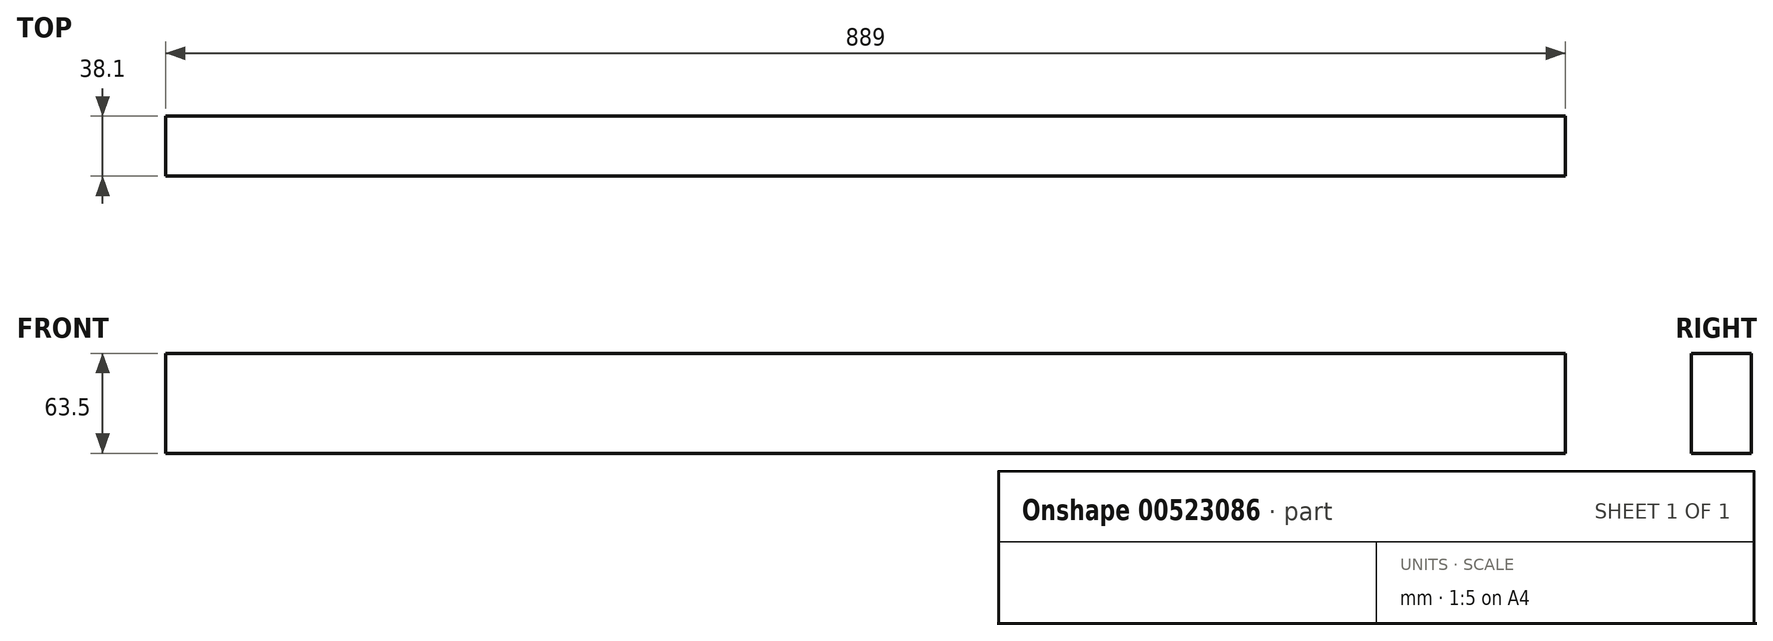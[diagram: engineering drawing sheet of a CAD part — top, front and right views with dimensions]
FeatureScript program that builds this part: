
annotation { "Feature Type Name" : "Feature", "Feature Type Description" : "" }
export const myFeature = defineFeature(function(context is Context, id is Id, definition is map)
    precondition{}
    {
        {
            var Q0;
            Q0=qCreatedBy(makeId("Top.planeOp"),FACE);
            var sketch = newSketch(context, id + "F0", { "sketchPlane" : qUnion([Q0])});
            skLineSegment(sketch, "E0.bottom", {"start": v(0, 0) * mm, "end": v(889, 0) * mm});
            skLineSegment(sketch, "E0.top", {"start": v(0, 38.1) * mm, "end": v(889, 38.1) * mm});
            skLineSegment(sketch, "E0.left", {"start": v(0, 0) * mm, "end": v(0, 38.1) * mm});
            skLineSegment(sketch, "E0.right", {"start": v(889, 0) * mm, "end": v(889, 38.1) * mm});
            skSolve(sketch);
        }
        {
            var Q0;
            Q0 = qSketchRegion(id + "F0", true);
            extrude(context, id + "F1", {"entities" : qUnion([Q0]), "depth" : 63.5 * mm, "offsetDistance" : 25.4 * mm});
        }
    });
